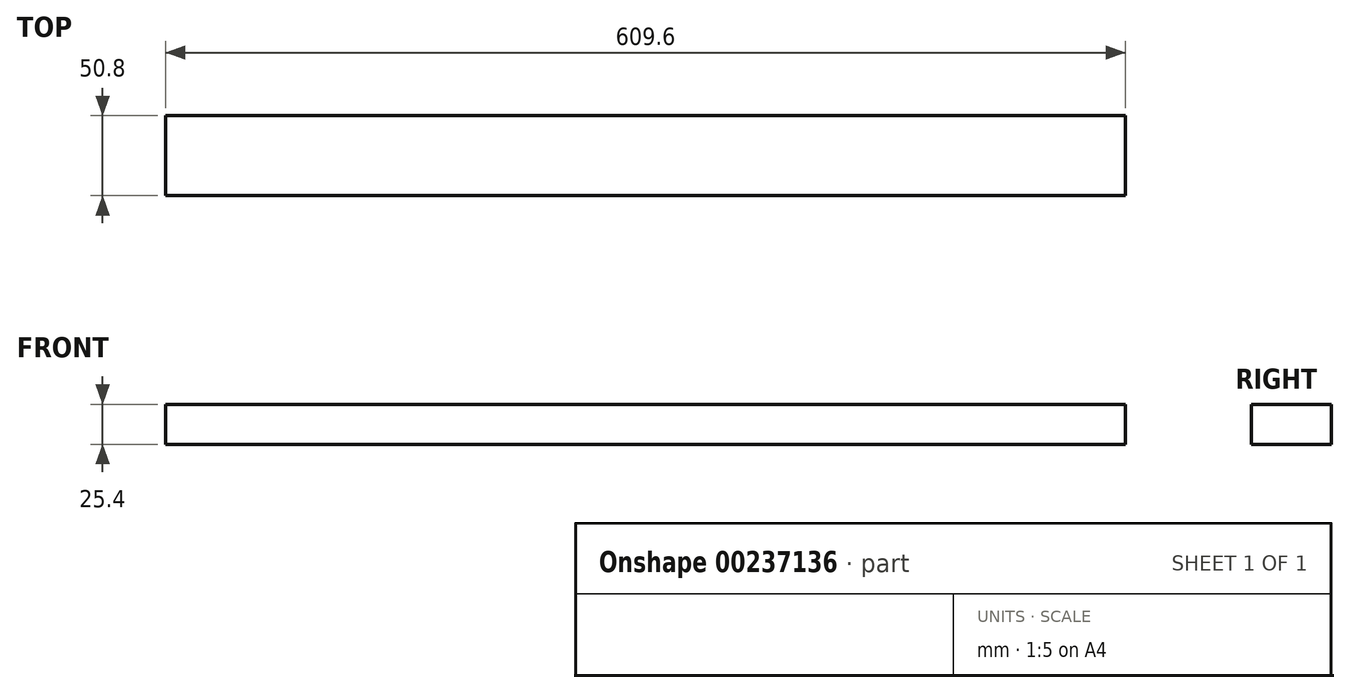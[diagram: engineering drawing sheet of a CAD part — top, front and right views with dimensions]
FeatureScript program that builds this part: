
annotation { "Feature Type Name" : "Feature", "Feature Type Description" : "" }
export const myFeature = defineFeature(function(context is Context, id is Id, definition is map)
    precondition{}
    {
        {
            var Q0;
            Q0=qCreatedBy(makeId("Top.planeOp"),FACE);
            var sketch = newSketch(context, id + "F0", { "sketchPlane" : qUnion([Q0])});
            skLineSegment(sketch, "E0.bottom", {"start": v(0, 0) * mm, "end": v(609.6, 0) * mm});
            skLineSegment(sketch, "E0.top", {"start": v(0, 50.8) * mm, "end": v(609.6, 50.8) * mm});
            skLineSegment(sketch, "E0.left", {"start": v(0, 0) * mm, "end": v(0, 50.8) * mm});
            skLineSegment(sketch, "E0.right", {"start": v(609.6, 0) * mm, "end": v(609.6, 50.8) * mm});
            skSolve(sketch);
        }
        {
            var Q0;
            Q0=makeQuery(id+"F0.imprint","IMPRINT",FACE,{"disambiguationData":[TD([[makeQuery(id+"F0.imprint","IMPRINT",EDGE,{"derivedFrom":sQuery(id+"F0.wireOp",EDGE,"E0.bottom")}),1.0]])]});
            extrude(context, id + "F1", {"entities" : qUnion([Q0]), "depth" : 25.4 * mm});
        }
    });
